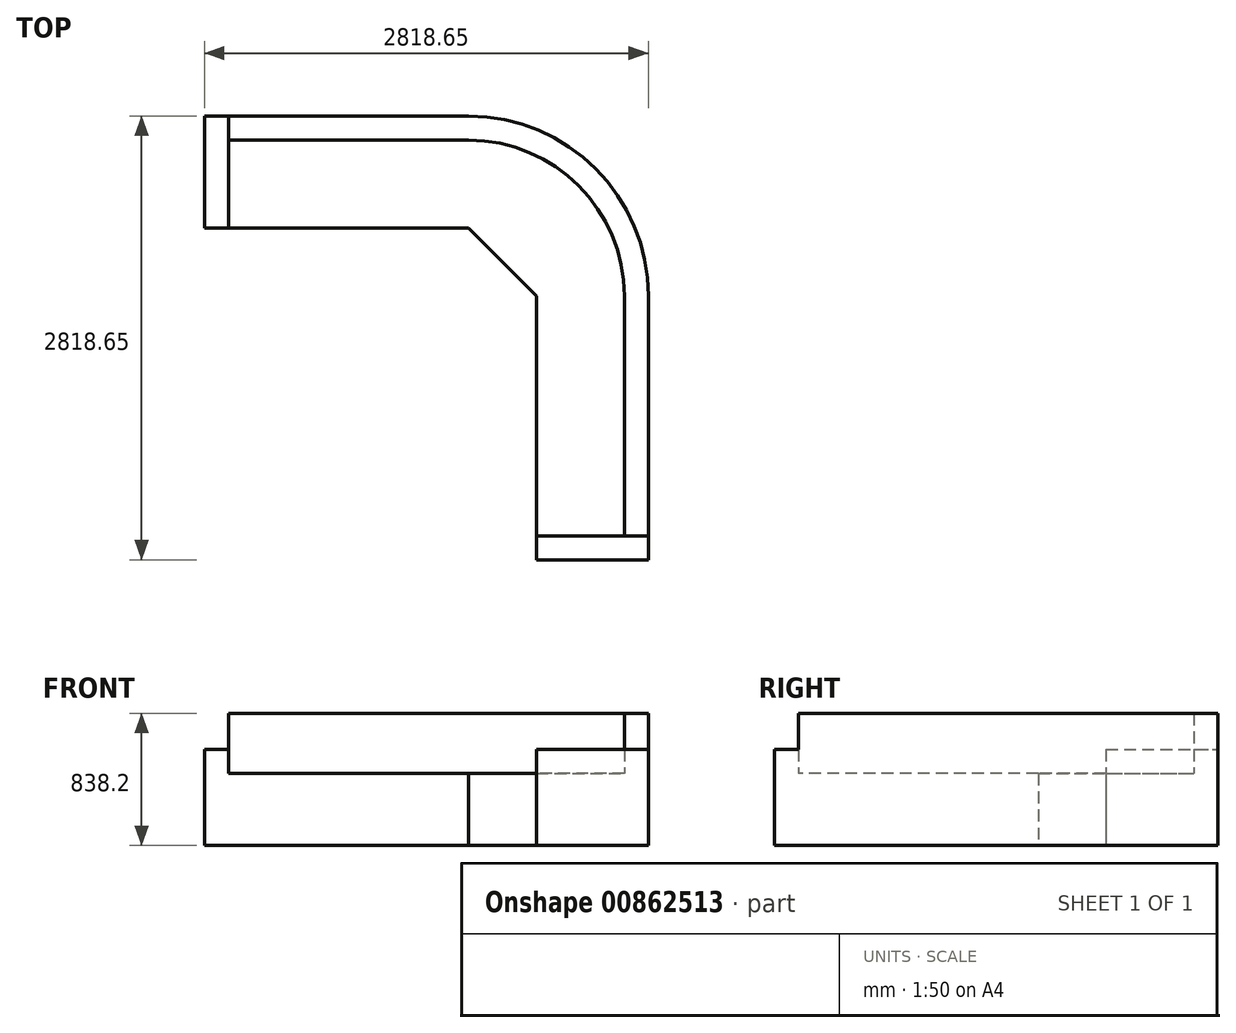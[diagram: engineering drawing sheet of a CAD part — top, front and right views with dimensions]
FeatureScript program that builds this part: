
annotation { "Feature Type Name" : "Feature", "Feature Type Description" : "" }
export const myFeature = defineFeature(function(context is Context, id is Id, definition is map)
    precondition{}
    {
        {
            var Q0;
            Q0=qCreatedBy(makeId("Top.planeOp"),FACE);
            var sketch = newSketch(context, id + "F0", { "sketchPlane" : qUnion([Q0])});
            skLineSegment(sketch, "E0.bottom", {"start": v(-431.05, 0) * mm, "end": v(-1955.05, 0) * mm});
            skLineSegment(sketch, "E0.top", {"start": v(-431.05, 558.8) * mm, "end": v(-1955.05, 558.8) * mm});
            skLineSegment(sketch, "E0.left", {"start": v(-431.05, 0) * mm, "end": v(-431.05, 558.8) * mm, "construction": true});
            skLineSegment(sketch, "E0.right", {"start": v(-1955.05, 0) * mm, "end": v(-1955.05, 558.8) * mm});
            skLineSegment(sketch, "E1.bottom", {"start": v(0, -431.05) * mm, "end": v(558.8, -431.05) * mm, "construction": true});
            skLineSegment(sketch, "E1.top", {"start": v(0, -1955.05) * mm, "end": v(558.8, -1955.05) * mm});
            skLineSegment(sketch, "E1.left", {"start": v(0, -431.05) * mm, "end": v(0, -1955.05) * mm});
            skLineSegment(sketch, "E1.right", {"start": v(558.8, -431.05) * mm, "end": v(558.8, -1955.05) * mm});
            skLineSegment(sketch, "E2", {"start": v(-431.05, 0) * mm, "end": v(0, -431.05) * mm});
            skArc(sketch, "E3", {"start": v(558.8, -431.05) * mm, "mid": v(268.88, 268.88) * mm, "end": v(-431.05, 558.8) * mm});
            skLineSegment(sketch, "E4", {"start": v(0, 0) * mm, "end": v(0, -431.05) * mm, "construction": true});
            skLineSegment(sketch, "E5", {"start": v(-431.05, 0) * mm, "end": v(0, 0) * mm, "construction": true});
            skSolve(sketch);
        }
        {
            var Q0;
            Q0 = qSketchRegion(id + "F0", true);
            extrude(context, id + "F1", {"entities" : qUnion([Q0]), "depth" : 457.2 * mm, "offsetDistance" : 25.4 * mm});
        }
        {
            var Q0;
            Q0=qCreatedBy(makeId("Top.planeOp"),FACE);
            var sketch = newSketch(context, id + "F2", { "sketchPlane" : qUnion([Q0])});
            skLineSegment(sketch, "E6.0", {"start": v(-431.05, 558.8) * mm, "end": v(-1955.05, 558.8) * mm});
            skArc(sketch, "E7.0", {"start": v(558.8, -431.05) * mm, "mid": v(268.88, 268.88) * mm, "end": v(-431.05, 558.8) * mm});
            skLineSegment(sketch, "E8.0", {"start": v(558.8, -431.05) * mm, "end": v(558.8, -1955.05) * mm});
            skLineSegment(sketch, "E9", {"start": v(-1955.05, 558.8) * mm, "end": v(-1955.05, 711.2) * mm});
            skLineSegment(sketch, "E10", {"start": v(-1955.05, 711.2) * mm, "end": v(-431.05, 711.2) * mm});
            skLineSegment(sketch, "E11", {"start": v(558.8, -1955.05) * mm, "end": v(711.2, -1955.05) * mm});
            skLineSegment(sketch, "E12", {"start": v(711.2, -1955.05) * mm, "end": v(711.2, -431.05) * mm});
            skArc(sketch, "E13", {"start": v(-431.05, 711.2) * mm, "mid": v(376.64, 376.64) * mm, "end": v(711.2, -431.05) * mm});
            skSolve(sketch);
        }
        {
            var Q0;
            Q0=makeQuery(id+"F2.imprint","IMPRINT",FACE,{"disambiguationData":[TD([[makeQuery(id+"F2.imprint","IMPRINT",EDGE,{"derivedFrom":sQuery(id+"F2.wireOp",EDGE,"E6.0")}),-1.0]])]});
            extrude(context, id + "F3", {"entities" : qUnion([Q0]), "operationType" : NewBodyOperationType.ADD, "depth" : 838.2 * mm, "offsetDistance" : 25.4 * mm});
        }
        {
            var Q0;
            Q0=qCreatedBy(makeId("Top.planeOp"),FACE);
            var sketch = newSketch(context, id + "F4", { "sketchPlane" : qUnion([Q0])});
            skLineSegment(sketch, "E14.bottom", {"start": v(-1955.05, 0) * mm, "end": v(-2107.45, 0) * mm});
            skLineSegment(sketch, "E14.top", {"start": v(-1955.05, 711.2) * mm, "end": v(-2107.45, 711.2) * mm});
            skLineSegment(sketch, "E14.left", {"start": v(-1955.05, 0) * mm, "end": v(-1955.05, 711.2) * mm});
            skLineSegment(sketch, "E14.right", {"start": v(-2107.45, 0) * mm, "end": v(-2107.45, 711.2) * mm});
            skLineSegment(sketch, "E15.bottom", {"start": v(0, -1955.05) * mm, "end": v(711.2, -1955.05) * mm});
            skLineSegment(sketch, "E15.top", {"start": v(0, -2107.45) * mm, "end": v(711.2, -2107.45) * mm});
            skLineSegment(sketch, "E15.left", {"start": v(0, -1955.05) * mm, "end": v(0, -2107.45) * mm});
            skLineSegment(sketch, "E15.right", {"start": v(711.2, -1955.05) * mm, "end": v(711.2, -2107.45) * mm});
            skSolve(sketch);
        }
        {
            var Q0;
            Q0 = qSketchRegion(id + "F4", true);
            extrude(context, id + "F5", {"entities" : qUnion([Q0]), "operationType" : NewBodyOperationType.ADD, "depth" : 609.6 * mm, "offsetDistance" : 25.4 * mm});
        }
    });
